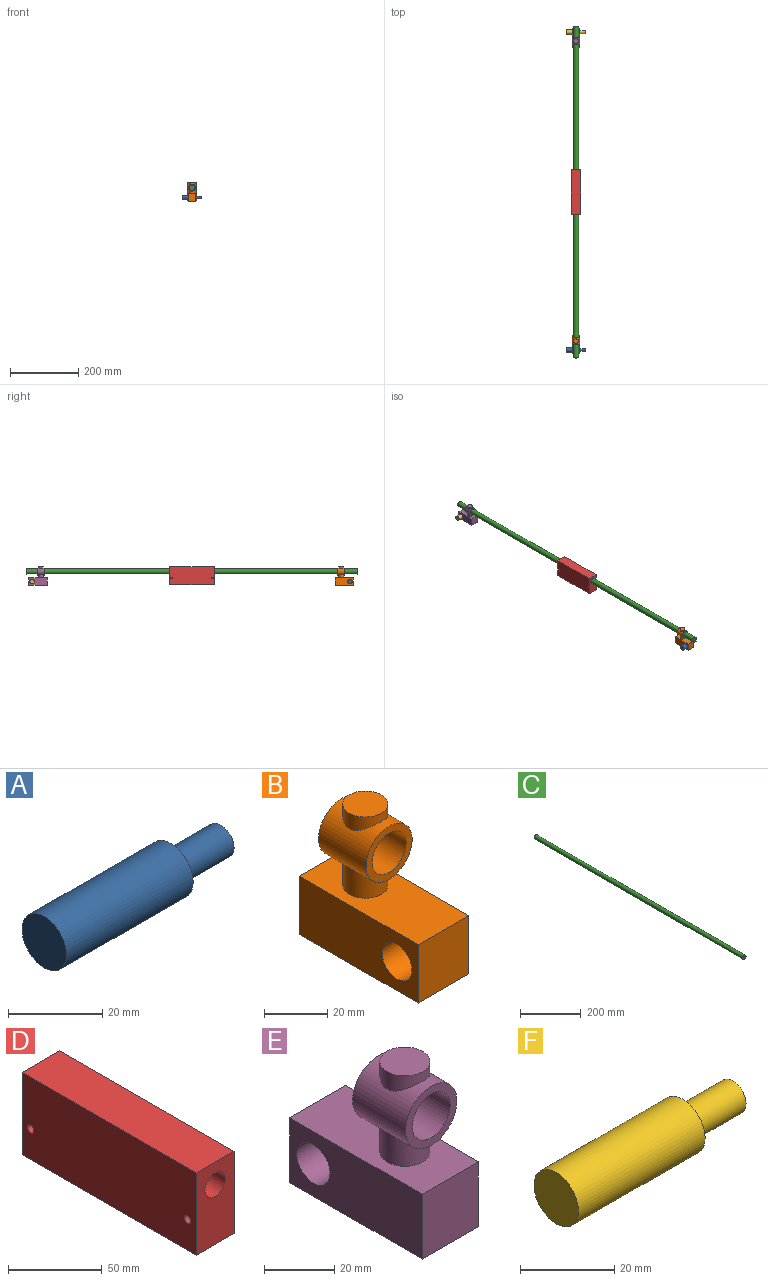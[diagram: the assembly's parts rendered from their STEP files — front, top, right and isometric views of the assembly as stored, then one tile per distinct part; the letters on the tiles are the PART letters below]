
ASSEMBLY  parts=6 mates=5
PART A: 5 faces, bbox 53.1x13.4x13.4 mm
  f0: cylinder r=6.69mm len=38.1mm, axis (-1,0,0), area 1602.3mm2, adj f1,f2
  f1: plane 13.39x13.39mm, normal (1,0,0), area 90.5mm2, adj f0,f3
  f2: plane 13.39x13.39mm, normal (-1,0,0), area 140.7mm2, adj f0
  f3: cylinder r=4mm len=15mm, axis (-1,0,0), area 377mm2, adj f1,f4
  f4: plane 8x8mm, normal (1,0,0), area 50.3mm2, adj f3
PART B: 18 faces, bbox 22.6x53.3x54.1 mm
  f0: plane 53.34x22.61mm, normal (0,0,1), area 1045.3mm2, adj f1,f4,f5,f6,f12
  f1: plane 22.61x22.61mm, normal (0,-1,0), area 511mm2, adj f0,f2,f5,f6
  f2: plane 53.34x22.61mm, normal (0,0,-1), area 1205.8mm2, adj f1,f4,f5,f6
  f3: cylinder r=6.69mm len=22.61mm, axis (-1,0,0), area 950.7mm2, adj f5,f6
  f4: plane 22.61x22.61mm, normal (0,1,0), area 511mm2, adj f0,f2,f5,f6
  f5: plane 53.34x22.61mm, normal (1,0,0), area 1065.1mm2, adj f0,f1,f2,f3,f4
  f6: plane 53.34x22.61mm, normal (-1,0,0), area 1065.1mm2, adj f0,f1,f2,f3,f4
  f7: cylinder r=10.34mm len=21.33mm, axis (0,1,0), area 1042.3mm2, adj f8,f10,f11,f12,f13,f14,f15,f16
  f8: plane 20.68x20.68mm, normal (0,-1,0), area 153.4mm2, adj f7,f9
  f9: cylinder r=7.62mm len=21.33mm, axis (0,1,0), area 1021.1mm2, adj f8,f10
  f10: plane 20.68x20.68mm, normal (0,1,0), area 153.4mm2, adj f7,f9
  f11: plane 3.01x0.16mm, normal (0,0,1), area 0.3mm2, adj f7,f12
  f12: cylinder r=7.15mm len=14.3mm, axis (0,0,-1), area 401.1mm2, adj f0,f7,f11,f13
  f13: plane 3.01x0.16mm, normal (0,0,1), area 0.3mm2, adj f7,f12
  f14: plane 3.01x0.16mm, normal (0,0,-1), area 0.3mm2, adj f7,f15
  f15: cylinder r=7.15mm len=14.3mm, axis (0,0,-1), area 208.3mm2, adj f7,f14,f16,f17
  f16: plane 3.01x0.16mm, normal (0,0,-1), area 0.3mm2, adj f7,f15
  f17: plane 14.3x14.3mm, normal (0,0,1), area 160.5mm2, adj f15
PART C: 3 faces, bbox 15.2x970.3x15.2 mm
  f0: cylinder r=7.62mm len=970.28mm, axis (0,1,0), area 46454.9mm2, adj f1,f2
  f1: plane 15.24x15.24mm, normal (0,1,0), area 182.4mm2, adj f0
  f2: plane 15.24x15.24mm, normal (0,-1,0), area 182.4mm2, adj f0
PART D: 9 faces, bbox 28.4x131.1x53.6 mm
  f0: plane 53.59x28.45mm, normal (0,1,0), area 1342.2mm2, adj f1,f4,f6,f7,f8
  f1: plane 131.06x28.45mm, normal (0,0,1), area 3728.5mm2, adj f0,f2,f6,f7
  f2: plane 53.59x28.45mm, normal (0,-1,0), area 1342.2mm2, adj f1,f4,f6,f7,f8
  f3: cylinder r=2.5mm len=28.45mm, axis (-1,0,0), area 447mm2, adj f6,f7
  f4: plane 131.06x28.45mm, normal (0,0,-1), area 3728.5mm2, adj f0,f2,f6,f7
  f5: cylinder r=2.5mm len=28.45mm, axis (-1,0,0), area 447mm2, adj f6,f7
  f6: plane 131.06x53.59mm, normal (1,0,0), area 6985mm2, adj f0,f1,f2,f3,f4,f5
  f7: plane 131.06x53.59mm, normal (-1,0,0), area 6985mm2, adj f0,f1,f2,f3,f4,f5
  f8: cylinder r=7.62mm len=131.06mm, axis (0,1,0), area 6275.1mm2, adj f0,f2
PART E: 18 faces, bbox 22.6x53.3x54.1 mm
  f0: cylinder r=10.34mm len=21.33mm, axis (0,1,0), area 1042.3mm2, adj f8,f9,f11,f12,f13,f14,f15,f16
  f1: plane 22.61x22.61mm, normal (0,1,0), area 511mm2, adj f2,f4,f6,f7
  f2: plane 53.34x22.61mm, normal (0,0,1), area 1045.3mm2, adj f1,f3,f6,f7,f13
  f3: plane 22.61x22.61mm, normal (0,-1,0), area 511mm2, adj f2,f4,f6,f7
  f4: plane 53.34x22.61mm, normal (0,0,-1), area 1205.8mm2, adj f1,f3,f6,f7
  f5: cylinder r=6.69mm len=22.61mm, axis (-1,0,0), area 950.7mm2, adj f6,f7
  f6: plane 53.34x22.61mm, normal (1,0,0), area 1065.1mm2, adj f1,f2,f3,f4,f5
  f7: plane 53.34x22.61mm, normal (-1,0,0), area 1065.1mm2, adj f1,f2,f3,f4,f5
  f8: plane 20.68x20.68mm, normal (0,1,0), area 153.4mm2, adj f0,f10
  f9: plane 20.68x20.68mm, normal (0,-1,0), area 153.4mm2, adj f0,f10
  f10: cylinder r=7.62mm len=21.33mm, axis (0,1,0), area 1021.1mm2, adj f8,f9
  f11: plane 3.01x0.16mm, normal (0,0,1), area 0.3mm2, adj f0,f13
  f12: plane 3.01x0.16mm, normal (0,0,1), area 0.3mm2, adj f0,f13
  f13: cylinder r=7.15mm len=14.3mm, axis (0,0,-1), area 401.2mm2, adj f0,f2,f11,f12
  f14: cylinder r=7.15mm len=14.3mm, axis (0,0,-1), area 208.3mm2, adj f0,f15,f16,f17
  f15: plane 3.01x0.16mm, normal (0,0,-1), area 0.3mm2, adj f0,f14
  f16: plane 3.01x0.16mm, normal (0,0,-1), area 0.3mm2, adj f0,f14
  f17: plane 14.3x14.3mm, normal (0,0,1), area 160.5mm2, adj f14
PART F: 5 faces, bbox 53.1x13.4x13.4 mm
  f0: cylinder r=6.69mm len=38.1mm, axis (-1,0,0), area 1602.3mm2, adj f1,f2
  f1: plane 13.39x13.39mm, normal (1,0,0), area 90.5mm2, adj f0,f3
  f2: plane 13.39x13.39mm, normal (-1,0,0), area 140.7mm2, adj f0
  f3: cylinder r=4mm len=15mm, axis (-1,0,0), area 377mm2, adj f1,f4
  f4: plane 8x8mm, normal (1,0,0), area 50.3mm2, adj f3
PLACE A t=(59.74,-263.55,28.69)mm
PLACE B t=(73.58,-263.55,28.69)mm
PLACE C t=(73.58,279.4,-61.99)mm
PLACE D t=(73.58,0,28.69)mm
PLACE E t=(73.58,268.85,28.69)mm
PLACE F t=(59.74,268.85,28.69)mm
MATE slider A.f0 <-> B.f3  axis (-1,0,0) through (47.04,-461.79,-0.52)mm
MATE slider C.f0 <-> D.f8  axis (0,1,0) through (73.58,0,28.69)mm
MATE slider E.f0 <-> C.f0  axis (0,1,0) through (73.58,452.24,28.69)mm
MATE slider B.f7 <-> C.f0  axis (0,-1,0) through (73.58,-446.93,28.69)mm
MATE slider F.f0 <-> E.f5  axis (-1,0,0) through (47.04,467.1,-0.52)mm
